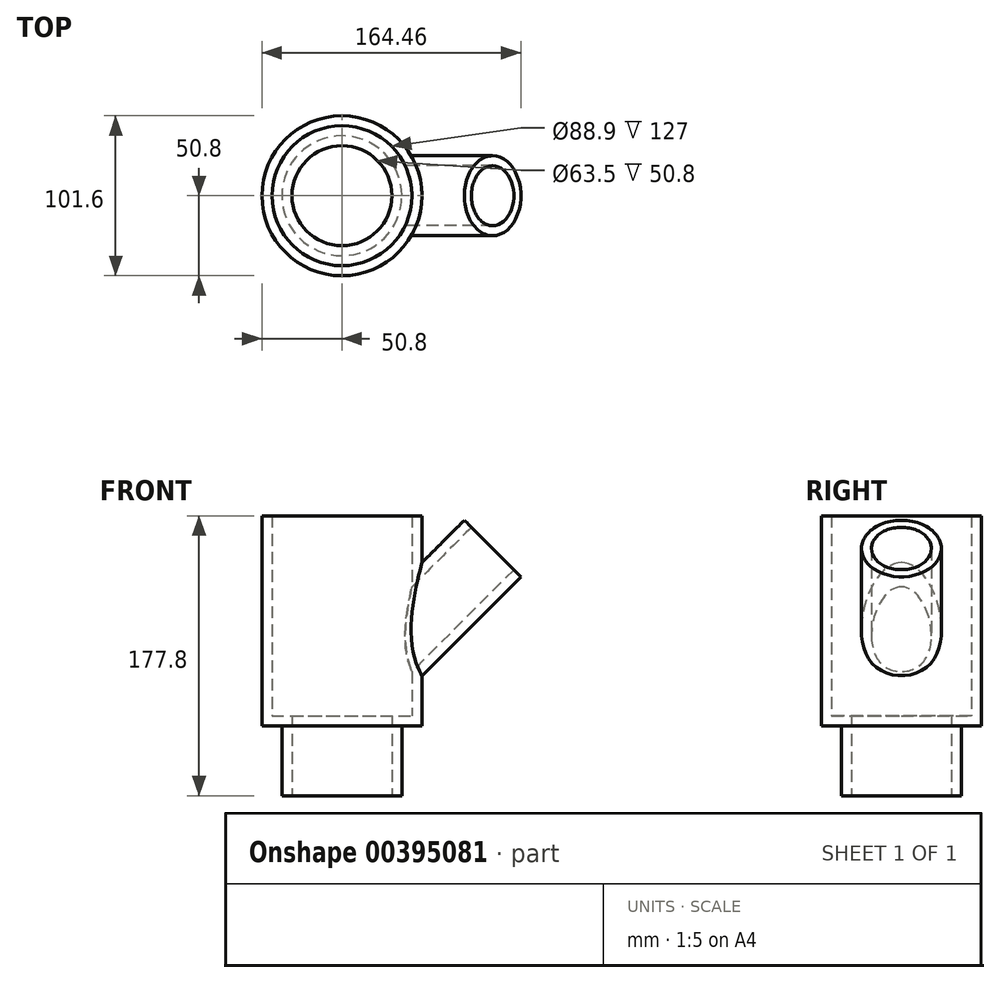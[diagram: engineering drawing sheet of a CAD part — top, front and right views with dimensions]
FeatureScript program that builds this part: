
annotation { "Feature Type Name" : "Feature", "Feature Type Description" : "" }
export const myFeature = defineFeature(function(context is Context, id is Id, definition is map)
    precondition{}
    {
        {
            var Q0;
            Q0=qCreatedBy(makeId("Front.planeOp"),FACE);
            var sketch = newSketch(context, id + "F0", { "sketchPlane" : qUnion([Q0])});
            skLineSegment(sketch, "E0", {"start": v(0, 0) * mm, "end": v(0, 177.8) * mm});
            skLineSegment(sketch, "E1", {"start": v(0, 177.8) * mm, "end": v(50.8, 177.8) * mm});
            skLineSegment(sketch, "E2", {"start": v(50.8, 177.8) * mm, "end": v(50.8, 44.45) * mm});
            skLineSegment(sketch, "E3", {"start": v(38.1, 0) * mm, "end": v(0, 0) * mm});
            skLineSegment(sketch, "E4", {"start": v(38.1, 0) * mm, "end": v(38.1, 44.45) * mm});
            skLineSegment(sketch, "E5", {"start": v(38.1, 44.45) * mm, "end": v(50.8, 44.45) * mm});
            skSolve(sketch);
        }
        {
            var Q0;
            Q0=qSketchRegion(id+"F0",true);
            var Q1;
            Q1=sQuery(id+"F0.wireOp",EDGE,"E0");
            revolve(context, id + "F1", {"entities" : qUnion([Q0]), "axis" : qUnion([Q1]), "revolveType" : RevolveType.FULL});
        }
        {
            var Q0;
            Q0=qCreatedBy(makeId("Front.planeOp"),FACE);
            var sketch = newSketch(context, id + "F2", { "sketchPlane" : qUnion([Q0])});
            skLineSegment(sketch, "E6", {"start": v(0, 61.32) * mm, "end": v(95.7, 157.02) * mm});
            skLineSegment(sketch, "E7", {"start": v(95.7, 157.02) * mm, "end": v(113.66, 139.06) * mm});
            skLineSegment(sketch, "E8", {"start": v(113.66, 139.06) * mm, "end": v(0, 25.4) * mm});
            skLineSegment(sketch, "E9", {"start": v(0, 25.4) * mm, "end": v(0, 61.32) * mm});
            skPoint(sketch, "E10", {"position": v(50.8, 76.2) * mm});
            skSolve(sketch);
        }
        {
            var Q0;
            Q0=qSketchRegion(id+"F2",true);
            var Q1;
            Q1=sQuery(id+"F2.wireOp",EDGE,"E6");
            revolve(context, id + "F3", {"operationType" : NewBodyOperationType.ADD, "entities" : qUnion([Q0]), "axis" : qUnion([Q1]), "revolveType" : RevolveType.FULL});
        }
        {
            var Q0;
            Q0=makeQuery(id+"F1.opRevolve","SWEPT_FACE",FACE,{"disambiguationData":[OSD([sQuery(id+"F0.wireOp",EDGE,"E1")])]});
            var Q1;
            Q1=makeQuery(id+"F3.opRevolve","SWEPT_FACE",FACE,{"disambiguationData":[OSD([sQuery(id+"F2.wireOp",EDGE,"E7")])]});
            var Q2;
            Q2=makeQuery(id+"F1.opRevolve","SWEPT_FACE",FACE,{"disambiguationData":[OSD([sQuery(id+"F0.wireOp",EDGE,"E3")])]});
            shell(context, id + "F4", {"entities" : qUnion([Q0, Q1, Q2]), "thickness" : 6.35 * mm});
        }
    });
